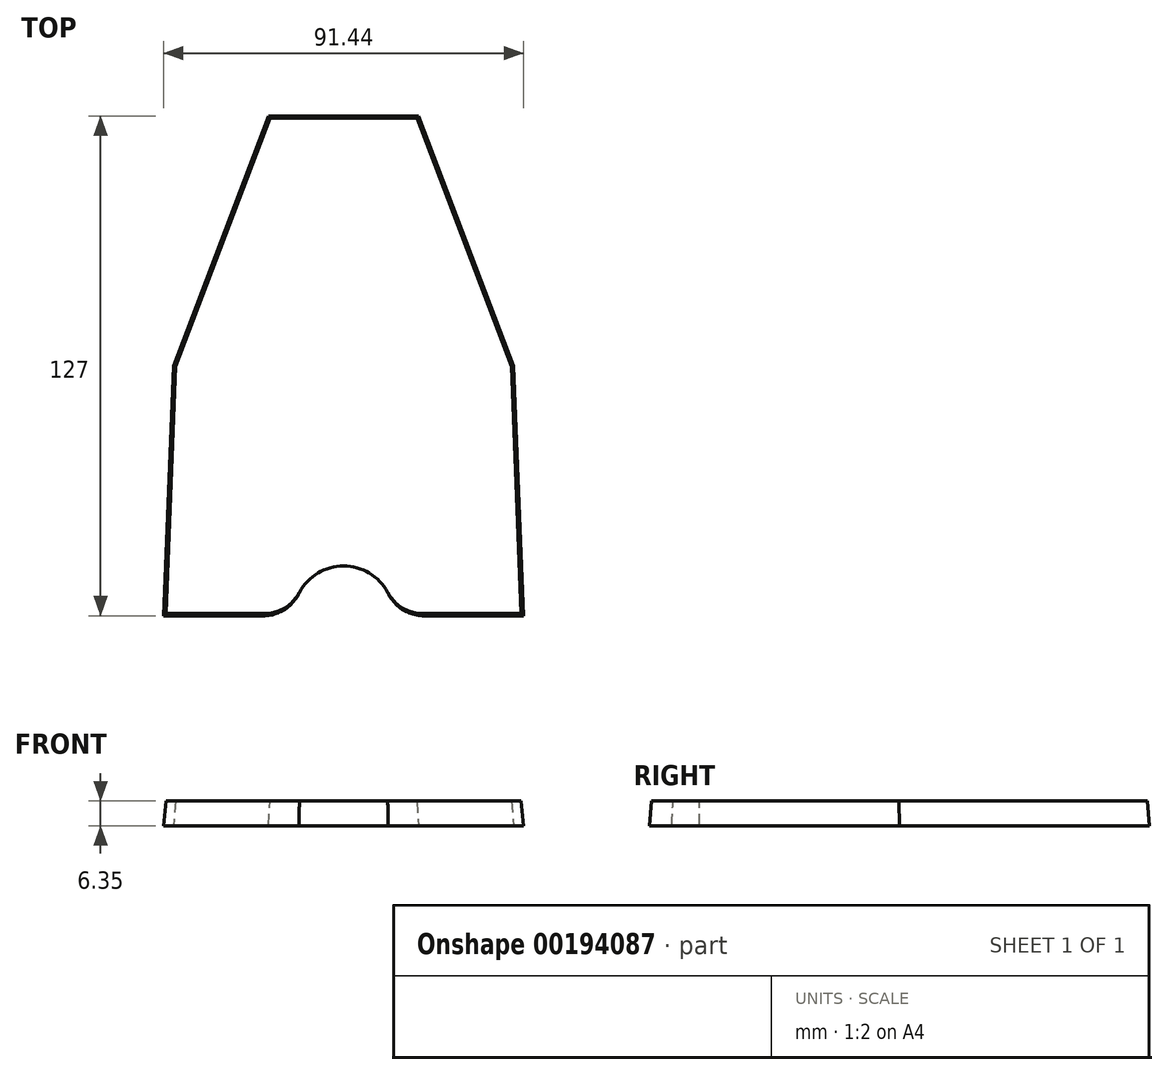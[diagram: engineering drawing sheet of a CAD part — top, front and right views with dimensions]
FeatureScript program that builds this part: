
annotation { "Feature Type Name" : "Feature", "Feature Type Description" : "" }
export const myFeature = defineFeature(function(context is Context, id is Id, definition is map)
    precondition{}
    {
        {
            var Q0;
            Q0=qCreatedBy(makeId("Top.planeOp"),FACE);
            var sketch = newSketch(context, id + "F0", { "sketchPlane" : qUnion([Q0])});
            skLineSegment(sketch, "E0", {"start": v(-45.72, 0) * mm, "end": v(45.72, 0) * mm});
            skLineSegment(sketch, "E1", {"start": v(45.72, 0) * mm, "end": v(43.18, 63.5) * mm});
            skLineSegment(sketch, "E2", {"start": v(43.18, 63.5) * mm, "end": v(19.05, 127) * mm});
            skLineSegment(sketch, "E3", {"start": v(19.05, 127) * mm, "end": v(-19.05, 127) * mm});
            skLineSegment(sketch, "E4", {"start": v(0, 0) * mm, "end": v(0, 95.69) * mm, "construction": true});
            skLineSegment(sketch, "E5.MirrorCS", {"start": v(-43.18, 63.5) * mm, "end": v(-19.05, 127) * mm});
            skLineSegment(sketch, "E6.MirrorCS", {"start": v(-45.72, 0) * mm, "end": v(-43.18, 63.5) * mm});
            skSolve(sketch);
        }
        {
            var Q0;
            Q0=makeQuery(id+"F0.imprint","IMPRINT",FACE,{"disambiguationData":[TD([[makeQuery(id+"F0.imprint","IMPRINT",EDGE,{"derivedFrom":sQuery(id+"F0.wireOp",EDGE,"E0")}),1.0]])]});
            extrude(context, id + "F1", {"entities" : qUnion([Q0]), "depth" : 6.35 * mm, "hasDraft" : true, "draftAngle" : 5 * degree, "draftPullDirection" : true});
        }
        {
            var Q0;
            Q0=makeQuery(id+"F1.opExtrude","CAP_FACE",FACE,{"disambiguationData":[OSD([sQuery(id+"F0.wireOp",EDGE,"E0"),sQuery(id+"F0.wireOp",EDGE,"E1"),sQuery(id+"F0.wireOp",EDGE,"E2"),sQuery(id+"F0.wireOp",EDGE,"E3"),sQuery(id+"F0.wireOp",EDGE,"E5.MirrorCS"),sQuery(id+"F0.wireOp",EDGE,"E6.MirrorCS")])],"isStart":false});
            var sketch = newSketch(context, id + "F2", { "sketchPlane" : qUnion([Q0])});
            skCircle(sketch, "E7", {"center": v(0, 0) * mm, "radius": 12.7 * mm});
            skSolve(sketch);
        }
        {
            var Q0;
            Q0 = qSketchRegion(id + "F2", true);
            extrude(context, id + "F3", {"entities" : qUnion([Q0]), "operationType" : NewBodyOperationType.REMOVE, "endBound" : BoundingType.THROUGH_ALL, "oppositeDirection" : true, "depth" : 25.4 * mm});
        }
        {
            var Q0;
            Q0=makeQuery(id+"F3.boolean.opBoolean","INTERSECT",EDGE,{"disambiguationData":[OD(0.0)],"derivedFrom":[makeQuery(id+"F1.opExtrude","SWEPT_FACE",FACE,{"disambiguationData":[OSD([sQuery(id+"F0.wireOp",EDGE,"E0")])]}),makeQuery(id+"F3.opExtrude","SWEPT_FACE",FACE,{"disambiguationData":[OSD([sQuery(id+"F2.wireOp",EDGE,"E7")])]})]});
            var Q1;
            Q1=makeQuery(id+"F3.boolean.opBoolean","INTERSECT",EDGE,{"disambiguationData":[OD(1.0)],"derivedFrom":[makeQuery(id+"F1.opExtrude","SWEPT_FACE",FACE,{"disambiguationData":[OSD([sQuery(id+"F0.wireOp",EDGE,"E0")])]}),makeQuery(id+"F3.opExtrude","SWEPT_FACE",FACE,{"disambiguationData":[OSD([sQuery(id+"F2.wireOp",EDGE,"E7")])]})]});
            fillet(context, id + "F4", {"entities" : qUnion([Q0, Q1]), "radius" : 10.16 * mm, "tangentPropagation" : true, "allowEdgeOverflow" : false});
        }
    });
